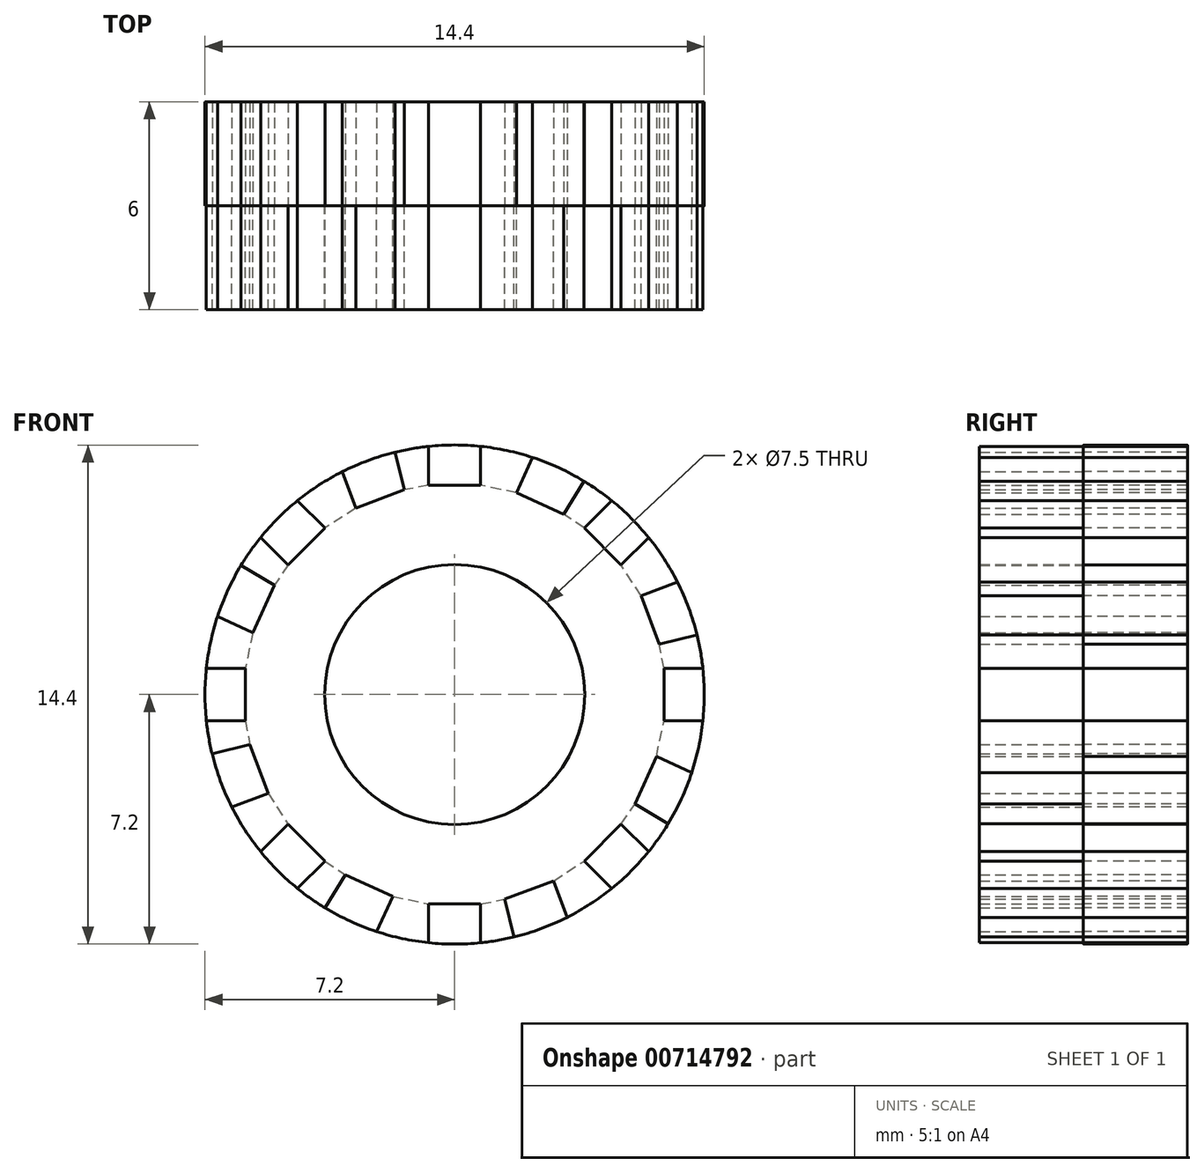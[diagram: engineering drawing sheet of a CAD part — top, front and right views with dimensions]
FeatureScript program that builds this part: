
annotation { "Feature Type Name" : "Feature", "Feature Type Description" : "" }
export const myFeature = defineFeature(function(context is Context, id is Id, definition is map)
    precondition{}
    {
        {
            var Q0;
            Q0=qCreatedBy(makeId("Front.planeOp"),FACE);
            var sketch = newSketch(context, id + "F0", { "sketchPlane" : qUnion([Q0])});
            skCircle(sketch, "E0", {"center": v(0, 0) * mm, "radius": 3.75 * mm});
            skArc(sketch, "E1", {"start": v(-0.75, 7.16) * mm, "mid": v(-1.23, 7.1) * mm, "end": v(-1.71, 7) * mm});
            skLineSegment(sketch, "E2", {"start": v(-0.75, 7.16) * mm, "end": v(-0.75, 6.04) * mm});
            skLineSegment(sketch, "E3", {"start": v(-0.75, 6.04) * mm, "end": v(0.75, 6.04) * mm});
            skLineSegment(sketch, "E4", {"start": v(0.75, 6.04) * mm, "end": v(0.75, 7.16) * mm});
            skLineSegment(sketch, "E5", {"start": v(2.25, 6.84) * mm, "end": v(1.79, 5.82) * mm});
            skLineSegment(sketch, "E6", {"start": v(1.79, 5.82) * mm, "end": v(3.15, 5.2) * mm});
            skLineSegment(sketch, "E7", {"start": v(3.15, 5.2) * mm, "end": v(3.73, 6.16) * mm});
            skArc(sketch, "E8.trimOffspring", {"start": v(2.25, 6.84) * mm, "mid": v(1.5, 7.04) * mm, "end": v(0.75, 7.16) * mm});
            skLineSegment(sketch, "E9.1.0", {"start": v(-5.6, 4.53) * mm, "end": v(-4.8, 3.74) * mm});
            skLineSegment(sketch, "E9.1.1", {"start": v(-4.8, 3.74) * mm, "end": v(-3.74, 4.8) * mm});
            skLineSegment(sketch, "E9.1.2", {"start": v(-3.74, 4.8) * mm, "end": v(-4.53, 5.6) * mm});
            skArc(sketch, "E9.1.3", {"start": v(-3.25, 6.43) * mm, "mid": v(-3.91, 6.04) * mm, "end": v(-4.53, 5.6) * mm});
            skLineSegment(sketch, "E9.1.4", {"start": v(-3.25, 6.43) * mm, "end": v(-2.85, 5.38) * mm});
            skLineSegment(sketch, "E9.1.5", {"start": v(-2.85, 5.38) * mm, "end": v(-1.45, 5.9) * mm});
            skLineSegment(sketch, "E9.1.6", {"start": v(-1.45, 5.9) * mm, "end": v(-1.71, 7) * mm});
            skLineSegment(sketch, "E9.2.0", {"start": v(-7.16, -0.75) * mm, "end": v(-6.04, -0.75) * mm});
            skLineSegment(sketch, "E9.2.1", {"start": v(-6.04, -0.75) * mm, "end": v(-6.04, 0.75) * mm});
            skLineSegment(sketch, "E9.2.2", {"start": v(-6.04, 0.75) * mm, "end": v(-7.16, 0.75) * mm});
            skArc(sketch, "E9.2.3", {"start": v(-6.84, 2.25) * mm, "mid": v(-7.04, 1.5) * mm, "end": v(-7.16, 0.75) * mm});
            skLineSegment(sketch, "E9.2.4", {"start": v(-6.84, 2.25) * mm, "end": v(-5.82, 1.79) * mm});
            skLineSegment(sketch, "E9.2.5", {"start": v(-5.82, 1.79) * mm, "end": v(-5.2, 3.15) * mm});
            skLineSegment(sketch, "E9.2.6", {"start": v(-5.2, 3.15) * mm, "end": v(-6.16, 3.73) * mm});
            skLineSegment(sketch, "E9.3.0", {"start": v(-4.53, -5.6) * mm, "end": v(-3.74, -4.8) * mm});
            skLineSegment(sketch, "E9.3.1", {"start": v(-3.74, -4.8) * mm, "end": v(-4.8, -3.74) * mm});
            skLineSegment(sketch, "E9.3.2", {"start": v(-4.8, -3.74) * mm, "end": v(-5.6, -4.53) * mm});
            skArc(sketch, "E9.3.3", {"start": v(-6.43, -3.25) * mm, "mid": v(-6.04, -3.91) * mm, "end": v(-5.6, -4.53) * mm});
            skLineSegment(sketch, "E9.3.4", {"start": v(-6.43, -3.25) * mm, "end": v(-5.38, -2.85) * mm});
            skLineSegment(sketch, "E9.3.5", {"start": v(-5.38, -2.85) * mm, "end": v(-5.9, -1.45) * mm});
            skLineSegment(sketch, "E9.3.6", {"start": v(-5.9, -1.45) * mm, "end": v(-7, -1.71) * mm});
            skLineSegment(sketch, "E9.4.0", {"start": v(0.75, -7.16) * mm, "end": v(0.75, -6.04) * mm});
            skLineSegment(sketch, "E9.4.1", {"start": v(0.75, -6.04) * mm, "end": v(-0.75, -6.04) * mm});
            skLineSegment(sketch, "E9.4.2", {"start": v(-0.75, -6.04) * mm, "end": v(-0.75, -7.16) * mm});
            skArc(sketch, "E9.4.3", {"start": v(-2.25, -6.84) * mm, "mid": v(-1.5, -7.04) * mm, "end": v(-0.75, -7.16) * mm});
            skLineSegment(sketch, "E9.4.4", {"start": v(-2.25, -6.84) * mm, "end": v(-1.79, -5.82) * mm});
            skLineSegment(sketch, "E9.4.5", {"start": v(-1.79, -5.82) * mm, "end": v(-3.15, -5.2) * mm});
            skLineSegment(sketch, "E9.4.6", {"start": v(-3.15, -5.2) * mm, "end": v(-3.73, -6.16) * mm});
            skLineSegment(sketch, "E9.5.0", {"start": v(5.6, -4.53) * mm, "end": v(4.8, -3.74) * mm});
            skLineSegment(sketch, "E9.5.1", {"start": v(4.8, -3.74) * mm, "end": v(3.74, -4.8) * mm});
            skLineSegment(sketch, "E9.5.2", {"start": v(3.74, -4.8) * mm, "end": v(4.53, -5.6) * mm});
            skArc(sketch, "E9.5.3", {"start": v(3.25, -6.43) * mm, "mid": v(3.91, -6.04) * mm, "end": v(4.53, -5.6) * mm});
            skLineSegment(sketch, "E9.5.4", {"start": v(3.25, -6.43) * mm, "end": v(2.85, -5.38) * mm});
            skLineSegment(sketch, "E9.5.5", {"start": v(2.85, -5.38) * mm, "end": v(1.45, -5.9) * mm});
            skLineSegment(sketch, "E9.5.6", {"start": v(1.45, -5.9) * mm, "end": v(1.71, -7) * mm});
            skLineSegment(sketch, "E9.6.0", {"start": v(7.16, 0.75) * mm, "end": v(6.04, 0.75) * mm});
            skLineSegment(sketch, "E9.6.1", {"start": v(6.04, 0.75) * mm, "end": v(6.04, -0.75) * mm});
            skLineSegment(sketch, "E9.6.2", {"start": v(6.04, -0.75) * mm, "end": v(7.16, -0.75) * mm});
            skArc(sketch, "E9.6.3", {"start": v(6.84, -2.25) * mm, "mid": v(7.04, -1.5) * mm, "end": v(7.16, -0.75) * mm});
            skLineSegment(sketch, "E9.6.4", {"start": v(6.84, -2.25) * mm, "end": v(5.82, -1.79) * mm});
            skLineSegment(sketch, "E9.6.5", {"start": v(5.82, -1.79) * mm, "end": v(5.2, -3.15) * mm});
            skLineSegment(sketch, "E9.6.6", {"start": v(5.2, -3.15) * mm, "end": v(6.16, -3.73) * mm});
            skLineSegment(sketch, "E9.7.0", {"start": v(4.53, 5.6) * mm, "end": v(3.74, 4.8) * mm});
            skLineSegment(sketch, "E9.7.1", {"start": v(3.74, 4.8) * mm, "end": v(4.8, 3.74) * mm});
            skLineSegment(sketch, "E9.7.2", {"start": v(4.8, 3.74) * mm, "end": v(5.6, 4.53) * mm});
            skArc(sketch, "E9.7.3", {"start": v(6.43, 3.25) * mm, "mid": v(6.04, 3.91) * mm, "end": v(5.6, 4.53) * mm});
            skLineSegment(sketch, "E9.7.4", {"start": v(6.43, 3.25) * mm, "end": v(5.38, 2.85) * mm});
            skLineSegment(sketch, "E9.7.5", {"start": v(5.38, 2.85) * mm, "end": v(5.9, 1.45) * mm});
            skLineSegment(sketch, "E9.7.6", {"start": v(5.9, 1.45) * mm, "end": v(7, 1.71) * mm});
            skArc(sketch, "E10.trimOffspring", {"start": v(4.53, 5.6) * mm, "mid": v(4.14, 5.89) * mm, "end": v(3.73, 6.16) * mm});
            skArc(sketch, "E11.trimOffspring", {"start": v(7.16, 0.75) * mm, "mid": v(7.1, 1.23) * mm, "end": v(7, 1.71) * mm});
            skArc(sketch, "E12.trimOffspring", {"start": v(5.6, -4.53) * mm, "mid": v(5.89, -4.14) * mm, "end": v(6.16, -3.73) * mm});
            skArc(sketch, "E13.trimOffspring", {"start": v(0.75, -7.16) * mm, "mid": v(1.23, -7.1) * mm, "end": v(1.71, -7) * mm});
            skArc(sketch, "E14.trimOffspring", {"start": v(-4.53, -5.6) * mm, "mid": v(-4.14, -5.89) * mm, "end": v(-3.73, -6.16) * mm});
            skArc(sketch, "E15.trimOffspring", {"start": v(-7.16, -0.75) * mm, "mid": v(-7.1, -1.23) * mm, "end": v(-7, -1.71) * mm});
            skArc(sketch, "E16.trimOffspring", {"start": v(-5.6, 4.53) * mm, "mid": v(-5.89, 4.14) * mm, "end": v(-6.16, 3.73) * mm});
            skSolve(sketch);
        }
        {
            var Q0;
            Q0 = qSketchRegion(id + "F0", true);
            extrude(context, id + "F1", {"entities" : qUnion([Q0]), "depth" : 3 * mm, "offsetDistance" : 25 * mm});
        }
        {
            var Q0;
            Q0=makeQuery(id+"F1.opExtrude","CAP_FACE",FACE,{"disambiguationData":[OSD([sQuery(id+"F0.wireOp",EDGE,"E0"),sQuery(id+"F0.wireOp",EDGE,"E1"),sQuery(id+"F0.wireOp",EDGE,"E2"),sQuery(id+"F0.wireOp",EDGE,"E3"),sQuery(id+"F0.wireOp",EDGE,"E4"),sQuery(id+"F0.wireOp",EDGE,"E5"),sQuery(id+"F0.wireOp",EDGE,"E6"),sQuery(id+"F0.wireOp",EDGE,"E7"),sQuery(id+"F0.wireOp",EDGE,"E8.trimOffspring"),sQuery(id+"F0.wireOp",EDGE,"E9.1.0"),sQuery(id+"F0.wireOp",EDGE,"E9.1.1"),sQuery(id+"F0.wireOp",EDGE,"E9.1.2"),sQuery(id+"F0.wireOp",EDGE,"E9.1.4"),sQuery(id+"F0.wireOp",EDGE,"E9.1.5"),sQuery(id+"F0.wireOp",EDGE,"E9.1.6"),sQuery(id+"F0.wireOp",EDGE,"E9.2.0"),sQuery(id+"F0.wireOp",EDGE,"E9.2.1"),sQuery(id+"F0.wireOp",EDGE,"E9.2.2"),sQuery(id+"F0.wireOp",EDGE,"E9.2.4"),sQuery(id+"F0.wireOp",EDGE,"E9.2.5"),sQuery(id+"F0.wireOp",EDGE,"E9.2.6"),sQuery(id+"F0.wireOp",EDGE,"E9.3.0"),sQuery(id+"F0.wireOp",EDGE,"E9.3.1"),sQuery(id+"F0.wireOp",EDGE,"E9.3.2"),sQuery(id+"F0.wireOp",EDGE,"E9.3.4"),sQuery(id+"F0.wireOp",EDGE,"E9.3.5"),sQuery(id+"F0.wireOp",EDGE,"E9.3.6"),sQuery(id+"F0.wireOp",EDGE,"E9.4.0"),sQuery(id+"F0.wireOp",EDGE,"E9.4.1"),sQuery(id+"F0.wireOp",EDGE,"E9.4.2"),sQuery(id+"F0.wireOp",EDGE,"E9.4.4"),sQuery(id+"F0.wireOp",EDGE,"E9.4.5"),sQuery(id+"F0.wireOp",EDGE,"E9.4.6"),sQuery(id+"F0.wireOp",EDGE,"E9.5.0"),sQuery(id+"F0.wireOp",EDGE,"E9.5.1"),sQuery(id+"F0.wireOp",EDGE,"E9.5.2"),sQuery(id+"F0.wireOp",EDGE,"E9.5.4"),sQuery(id+"F0.wireOp",EDGE,"E9.5.5"),sQuery(id+"F0.wireOp",EDGE,"E9.5.6"),sQuery(id+"F0.wireOp",EDGE,"E9.6.0"),sQuery(id+"F0.wireOp",EDGE,"E9.6.1"),sQuery(id+"F0.wireOp",EDGE,"E9.6.2"),sQuery(id+"F0.wireOp",EDGE,"E9.6.4"),sQuery(id+"F0.wireOp",EDGE,"E9.6.5"),sQuery(id+"F0.wireOp",EDGE,"E9.6.6"),sQuery(id+"F0.wireOp",EDGE,"E9.7.0"),sQuery(id+"F0.wireOp",EDGE,"E9.7.1"),sQuery(id+"F0.wireOp",EDGE,"E9.7.2"),sQuery(id+"F0.wireOp",EDGE,"E9.7.4"),sQuery(id+"F0.wireOp",EDGE,"E9.7.5"),sQuery(id+"F0.wireOp",EDGE,"E9.7.6"),sQuery(id+"F0.wireOp",EDGE,"E10.trimOffspring"),sQuery(id+"F0.wireOp",EDGE,"E9.7.3"),sQuery(id+"F0.wireOp",EDGE,"E11.trimOffspring"),sQuery(id+"F0.wireOp",EDGE,"E9.6.3"),sQuery(id+"F0.wireOp",EDGE,"E12.trimOffspring"),sQuery(id+"F0.wireOp",EDGE,"E9.5.3"),sQuery(id+"F0.wireOp",EDGE,"E13.trimOffspring"),sQuery(id+"F0.wireOp",EDGE,"E9.4.3"),sQuery(id+"F0.wireOp",EDGE,"E14.trimOffspring"),sQuery(id+"F0.wireOp",EDGE,"E9.3.3"),sQuery(id+"F0.wireOp",EDGE,"E15.trimOffspring"),sQuery(id+"F0.wireOp",EDGE,"E9.2.3"),sQuery(id+"F0.wireOp",EDGE,"E16.trimOffspring"),sQuery(id+"F0.wireOp",EDGE,"E9.1.3")])],"isStart":true});
            var sketch = newSketch(context, id + "F2", { "sketchPlane" : qUnion([Q0])});
            skCircle(sketch, "E17", {"center": v(0, 0) * mm, "radius": 3.75 * mm});
            skArc(sketch, "E18", {"start": v(-2.25, 6.84) * mm, "mid": v(-3.01, 6.54) * mm, "end": v(-3.73, 6.16) * mm});
            skLineSegment(sketch, "E19", {"start": v(-2.25, 6.84) * mm, "end": v(-1.79, 5.82) * mm});
            skLineSegment(sketch, "E20", {"start": v(-1.79, 5.82) * mm, "end": v(-0.75, 6.04) * mm});
            skLineSegment(sketch, "E21", {"start": v(-0.75, 6.04) * mm, "end": v(-0.75, 7.16) * mm});
            skLineSegment(sketch, "E22", {"start": v(0.75, 7.16) * mm, "end": v(0.75, 6.04) * mm});
            skLineSegment(sketch, "E23", {"start": v(0.75, 6.04) * mm, "end": v(1.45, 5.9) * mm});
            skLineSegment(sketch, "E24", {"start": v(1.45, 5.9) * mm, "end": v(1.71, 7) * mm});
            skArc(sketch, "E25.trimOffspring", {"start": v(0.75, 7.16) * mm, "mid": v(0, 7.2) * mm, "end": v(-0.75, 7.16) * mm});
            skLineSegment(sketch, "E26.1.0", {"start": v(-6.43, 3.25) * mm, "end": v(-5.38, 2.85) * mm});
            skLineSegment(sketch, "E26.1.1", {"start": v(-5.38, 2.85) * mm, "end": v(-4.8, 3.74) * mm});
            skLineSegment(sketch, "E26.1.2", {"start": v(-4.8, 3.74) * mm, "end": v(-5.6, 4.53) * mm});
            skArc(sketch, "E26.1.3", {"start": v(-4.53, 5.6) * mm, "mid": v(-5.1, 5.1) * mm, "end": v(-5.6, 4.53) * mm});
            skLineSegment(sketch, "E26.1.4", {"start": v(-4.53, 5.6) * mm, "end": v(-3.74, 4.8) * mm});
            skLineSegment(sketch, "E26.1.5", {"start": v(-3.74, 4.8) * mm, "end": v(-3.15, 5.2) * mm});
            skLineSegment(sketch, "E26.1.6", {"start": v(-3.15, 5.2) * mm, "end": v(-3.73, 6.16) * mm});
            skLineSegment(sketch, "E26.2.0", {"start": v(-6.84, -2.25) * mm, "end": v(-5.82, -1.79) * mm});
            skLineSegment(sketch, "E26.2.1", {"start": v(-5.82, -1.79) * mm, "end": v(-6.04, -0.75) * mm});
            skLineSegment(sketch, "E26.2.2", {"start": v(-6.04, -0.75) * mm, "end": v(-7.16, -0.75) * mm});
            skArc(sketch, "E26.2.3", {"start": v(-7.16, 0.75) * mm, "mid": v(-7.2, 0) * mm, "end": v(-7.16, -0.75) * mm});
            skLineSegment(sketch, "E26.2.4", {"start": v(-7.16, 0.75) * mm, "end": v(-6.04, 0.75) * mm});
            skLineSegment(sketch, "E26.2.5", {"start": v(-6.04, 0.75) * mm, "end": v(-5.9, 1.45) * mm});
            skLineSegment(sketch, "E26.2.6", {"start": v(-5.9, 1.45) * mm, "end": v(-7, 1.71) * mm});
            skLineSegment(sketch, "E26.3.0", {"start": v(-3.25, -6.43) * mm, "end": v(-2.85, -5.38) * mm});
            skLineSegment(sketch, "E26.3.1", {"start": v(-2.85, -5.38) * mm, "end": v(-3.74, -4.8) * mm});
            skLineSegment(sketch, "E26.3.2", {"start": v(-3.74, -4.8) * mm, "end": v(-4.53, -5.6) * mm});
            skArc(sketch, "E26.3.3", {"start": v(-5.6, -4.53) * mm, "mid": v(-5.1, -5.1) * mm, "end": v(-4.53, -5.6) * mm});
            skLineSegment(sketch, "E26.3.4", {"start": v(-5.6, -4.53) * mm, "end": v(-4.8, -3.74) * mm});
            skLineSegment(sketch, "E26.3.5", {"start": v(-4.8, -3.74) * mm, "end": v(-5.2, -3.15) * mm});
            skLineSegment(sketch, "E26.3.6", {"start": v(-5.2, -3.15) * mm, "end": v(-6.16, -3.73) * mm});
            skLineSegment(sketch, "E26.4.0", {"start": v(2.25, -6.84) * mm, "end": v(1.79, -5.82) * mm});
            skLineSegment(sketch, "E26.4.1", {"start": v(1.79, -5.82) * mm, "end": v(0.75, -6.04) * mm});
            skLineSegment(sketch, "E26.4.2", {"start": v(0.75, -6.04) * mm, "end": v(0.75, -7.16) * mm});
            skArc(sketch, "E26.4.3", {"start": v(-0.75, -7.16) * mm, "mid": v(0, -7.2) * mm, "end": v(0.75, -7.16) * mm});
            skLineSegment(sketch, "E26.4.4", {"start": v(-0.75, -7.16) * mm, "end": v(-0.75, -6.04) * mm});
            skLineSegment(sketch, "E26.4.5", {"start": v(-0.75, -6.04) * mm, "end": v(-1.45, -5.9) * mm});
            skLineSegment(sketch, "E26.4.6", {"start": v(-1.45, -5.9) * mm, "end": v(-1.71, -7) * mm});
            skLineSegment(sketch, "E26.5.0", {"start": v(6.43, -3.25) * mm, "end": v(5.38, -2.85) * mm});
            skLineSegment(sketch, "E26.5.1", {"start": v(5.38, -2.85) * mm, "end": v(4.8, -3.74) * mm});
            skLineSegment(sketch, "E26.5.2", {"start": v(4.8, -3.74) * mm, "end": v(5.6, -4.53) * mm});
            skArc(sketch, "E26.5.3", {"start": v(4.53, -5.6) * mm, "mid": v(5.1, -5.1) * mm, "end": v(5.6, -4.53) * mm});
            skLineSegment(sketch, "E26.5.4", {"start": v(4.53, -5.6) * mm, "end": v(3.74, -4.8) * mm});
            skLineSegment(sketch, "E26.5.5", {"start": v(3.74, -4.8) * mm, "end": v(3.15, -5.2) * mm});
            skLineSegment(sketch, "E26.5.6", {"start": v(3.15, -5.2) * mm, "end": v(3.73, -6.16) * mm});
            skLineSegment(sketch, "E26.6.0", {"start": v(6.84, 2.25) * mm, "end": v(5.82, 1.79) * mm});
            skLineSegment(sketch, "E26.6.1", {"start": v(5.82, 1.79) * mm, "end": v(6.04, 0.75) * mm});
            skLineSegment(sketch, "E26.6.2", {"start": v(6.04, 0.75) * mm, "end": v(7.16, 0.75) * mm});
            skArc(sketch, "E26.6.3", {"start": v(7.16, -0.75) * mm, "mid": v(7.2, 0) * mm, "end": v(7.16, 0.75) * mm});
            skLineSegment(sketch, "E26.6.4", {"start": v(7.16, -0.75) * mm, "end": v(6.04, -0.75) * mm});
            skLineSegment(sketch, "E26.6.5", {"start": v(6.04, -0.75) * mm, "end": v(5.9, -1.45) * mm});
            skLineSegment(sketch, "E26.6.6", {"start": v(5.9, -1.45) * mm, "end": v(7, -1.71) * mm});
            skLineSegment(sketch, "E26.7.0", {"start": v(3.25, 6.43) * mm, "end": v(2.85, 5.38) * mm});
            skLineSegment(sketch, "E26.7.1", {"start": v(2.85, 5.38) * mm, "end": v(3.74, 4.8) * mm});
            skLineSegment(sketch, "E26.7.2", {"start": v(3.74, 4.8) * mm, "end": v(4.53, 5.6) * mm});
            skArc(sketch, "E26.7.3", {"start": v(5.6, 4.53) * mm, "mid": v(5.1, 5.1) * mm, "end": v(4.53, 5.6) * mm});
            skLineSegment(sketch, "E26.7.4", {"start": v(5.6, 4.53) * mm, "end": v(4.8, 3.74) * mm});
            skLineSegment(sketch, "E26.7.5", {"start": v(4.8, 3.74) * mm, "end": v(5.2, 3.15) * mm});
            skLineSegment(sketch, "E26.7.6", {"start": v(5.2, 3.15) * mm, "end": v(6.16, 3.73) * mm});
            skArc(sketch, "E27.trimOffspring", {"start": v(3.25, 6.43) * mm, "mid": v(2.5, 6.75) * mm, "end": v(1.71, 7) * mm});
            skArc(sketch, "E28.trimOffspring", {"start": v(6.84, 2.25) * mm, "mid": v(6.54, 3.01) * mm, "end": v(6.16, 3.73) * mm});
            skArc(sketch, "E29.trimOffspring", {"start": v(6.43, -3.25) * mm, "mid": v(6.75, -2.5) * mm, "end": v(7, -1.71) * mm});
            skArc(sketch, "E30.trimOffspring", {"start": v(2.25, -6.84) * mm, "mid": v(3.01, -6.54) * mm, "end": v(3.73, -6.16) * mm});
            skArc(sketch, "E31.trimOffspring", {"start": v(-3.25, -6.43) * mm, "mid": v(-2.5, -6.75) * mm, "end": v(-1.71, -7) * mm});
            skArc(sketch, "E32.trimOffspring", {"start": v(-6.84, -2.25) * mm, "mid": v(-6.54, -3.01) * mm, "end": v(-6.16, -3.73) * mm});
            skArc(sketch, "E33.trimOffspring", {"start": v(-6.43, 3.25) * mm, "mid": v(-6.75, 2.5) * mm, "end": v(-7, 1.71) * mm});
            skSolve(sketch);
        }
        {
            var Q0;
            Q0 = qSketchRegion(id + "F2", true);
            extrude(context, id + "F3", {"entities" : qUnion([Q0]), "depth" : 3 * mm, "offsetDistance" : 25 * mm});
        }
    });
